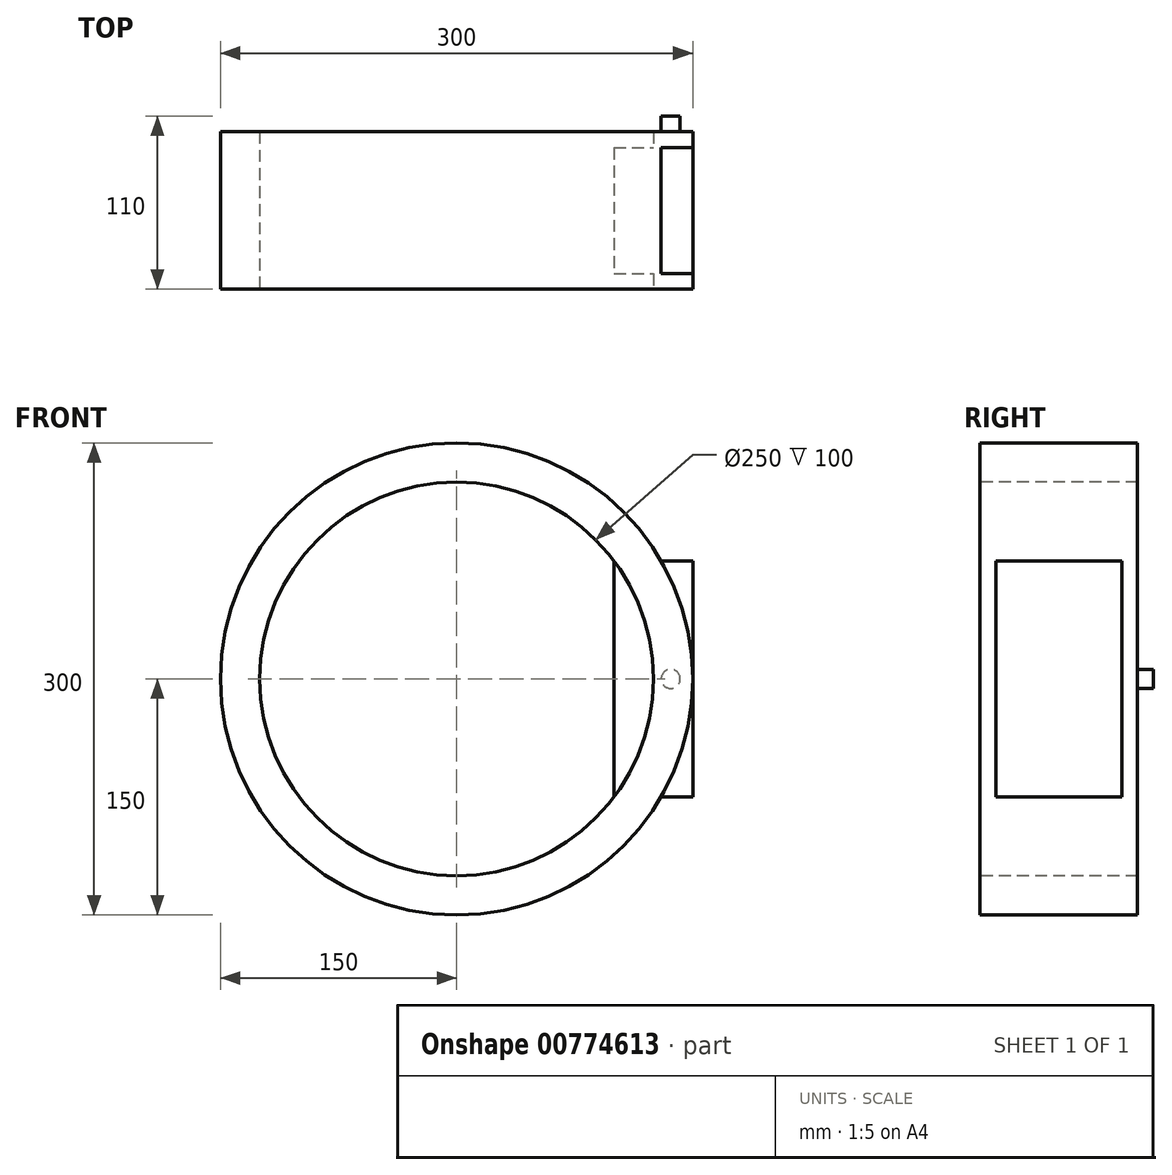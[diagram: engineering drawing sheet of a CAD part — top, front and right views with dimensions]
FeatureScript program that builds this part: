
annotation { "Feature Type Name" : "Feature", "Feature Type Description" : "" }
export const myFeature = defineFeature(function(context is Context, id is Id, definition is map)
    precondition{}
    {
        {
            var Q0;
            Q0=qCreatedBy(makeId("Front.planeOp"),FACE);
            var sketch = newSketch(context, id + "F0", { "sketchPlane" : qUnion([Q0])});
            skCircle(sketch, "E0", {"center": v(0, 0) * mm, "radius": 150 * mm});
            skSolve(sketch);
        }
        {
            var Q0;
            Q0=makeQuery(id+"F0.imprint","IMPRINT",FACE,{"disambiguationData":[TD([[makeQuery(id+"F0.imprint","IMPRINT",EDGE,{"derivedFrom":sQuery(id+"F0.wireOp",EDGE,"E0")}),1.0]])]});
            extrude(context, id + "F1", {"entities" : qUnion([Q0]), "endBound" : BoundingType.SYMMETRIC, "depth" : 100 * mm, "offsetDistance" : 25 * mm});
        }
        {
            var Q0;
            Q0=makeQuery(id+"F1.opExtrude","CAP_FACE",FACE,{"disambiguationData":[OSD([sQuery(id+"F0.wireOp",EDGE,"E0")])],"isStart":false});
            var sketch = newSketch(context, id + "F2", { "sketchPlane" : qUnion([Q0])});
            skCircle(sketch, "E1", {"center": v(0, 0) * mm, "radius": 125 * mm});
            skSolve(sketch);
        }
        {
            var Q0;
            Q0 = qSketchRegion(id + "F2", true);
            var Q1;
            Q1=makeQuery(id+"F1.opExtrude","CAP_FACE",FACE,{"disambiguationData":[OSD([sQuery(id+"F0.wireOp",EDGE,"E0")])],"isStart":true});
            extrude(context, id + "F3", {"entities" : qUnion([Q0]), "operationType" : NewBodyOperationType.REMOVE, "endBound" : BoundingType.UP_TO_SURFACE, "oppositeDirection" : true, "depth" : 25 * mm, "endBoundEntityFace" : qUnion([Q1]), "offsetDistance" : 25 * mm});
        }
        {
            var Q0;
            Q0=qCreatedBy(makeId("Right.planeOp"),FACE);
            var sketch = newSketch(context, id + "F4", { "sketchPlane" : qUnion([Q0])});
            skLineSegment(sketch, "E2.bottom", {"start": v(-40, 75) * mm, "end": v(40, 75) * mm});
            skLineSegment(sketch, "E2.top", {"start": v(-40, -75) * mm, "end": v(40, -75) * mm});
            skLineSegment(sketch, "E2.left", {"start": v(-40, 75) * mm, "end": v(-40, -75) * mm});
            skLineSegment(sketch, "E2.right", {"start": v(40, 75) * mm, "end": v(40, -75) * mm});
            skSolve(sketch);
        }
        {
            var Q0;
            Q0=makeQuery(id+"F4.imprint","IMPRINT",FACE,{"disambiguationData":[TD([[makeQuery(id+"F4.imprint","IMPRINT",EDGE,{"derivedFrom":sQuery(id+"F4.wireOp",EDGE,"E2.bottom")}),-1.0]])]});
            extrude(context, id + "F5", {"entities" : qUnion([Q0]), "operationType" : NewBodyOperationType.ADD, "depth" : 150 * mm, "offsetDistance" : 25 * mm});
        }
        {
            var Q0;
            Q0=makeQuery(id+"F5.opExtrude","CAP_FACE",FACE,{"disambiguationData":[OSD([sQuery(id+"F4.wireOp",EDGE,"E2.bottom"),sQuery(id+"F4.wireOp",EDGE,"E2.top"),sQuery(id+"F4.wireOp",EDGE,"E2.left"),sQuery(id+"F4.wireOp",EDGE,"E2.right")])],"isStart":true});
            var sketch = newSketch(context, id + "F6", { "sketchPlane" : qUnion([Q0])});
            skLineSegment(sketch, "E3.bottom", {"start": v(40, -75) * mm, "end": v(-40, -75) * mm});
            skLineSegment(sketch, "E3.top", {"start": v(40, 75) * mm, "end": v(-40, 75) * mm});
            skLineSegment(sketch, "E3.left", {"start": v(40, -75) * mm, "end": v(40, 75) * mm});
            skLineSegment(sketch, "E3.right", {"start": v(-40, -75) * mm, "end": v(-40, 75) * mm});
            skPoint(sketch, "E3.middle", {"position": v(0, 0) * mm});
            skSolve(sketch);
        }
        {
            var Q0;
            Q0 = qSketchRegion(id + "F6", true);
            extrude(context, id + "F7", {"entities" : qUnion([Q0]), "operationType" : NewBodyOperationType.REMOVE, "oppositeDirection" : true, "depth" : 100 * mm, "offsetDistance" : 25 * mm});
        }
        {
            var Q0;
            Q0=makeQuery(id+"F1.opExtrude","CAP_FACE",FACE,{"disambiguationData":[OSD([sQuery(id+"F0.wireOp",EDGE,"E0")])],"isStart":true});
            var sketch = newSketch(context, id + "F8", { "sketchPlane" : qUnion([Q0])});
            skCircle(sketch, "E4", {"center": v(-136, 0) * mm, "radius": 6.05 * mm});
            skSolve(sketch);
        }
        {
            var Q0;
            Q0 = qSketchRegion(id + "F8", true);
            extrude(context, id + "F9", {"entities" : qUnion([Q0]), "operationType" : NewBodyOperationType.ADD, "depth" : 10 * mm, "offsetDistance" : 25 * mm});
        }
    });
